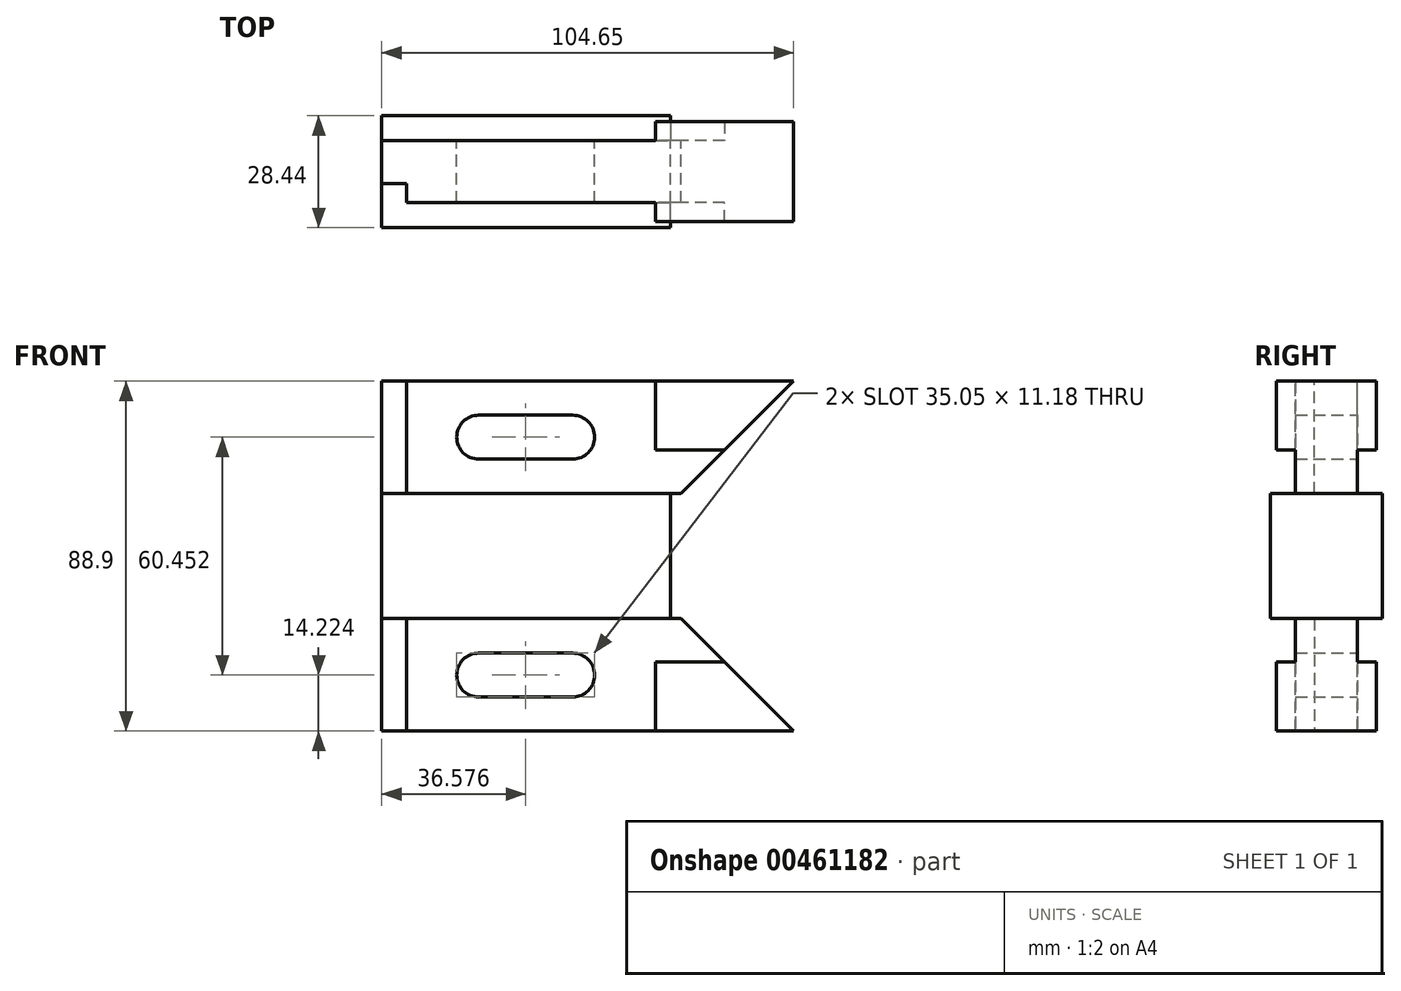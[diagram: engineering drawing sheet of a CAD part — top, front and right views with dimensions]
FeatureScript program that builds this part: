
annotation { "Feature Type Name" : "Feature", "Feature Type Description" : "" }
export const myFeature = defineFeature(function(context is Context, id is Id, definition is map)
    precondition{}
    {
        {
            var Q0;
            Q0=qCreatedBy(makeId("Front.planeOp"),FACE);
            var sketch = newSketch(context, id + "F0", { "sketchPlane" : qUnion([Q0])});
            skLineSegment(sketch, "E0", {"start": v(0, 0) * mm, "end": v(0, 44.45) * mm});
            skLineSegment(sketch, "E1", {"start": v(0, 44.45) * mm, "end": v(104.65, 44.45) * mm});
            skLineSegment(sketch, "E2", {"start": v(104.65, 44.45) * mm, "end": v(76.07, 15.88) * mm});
            skLineSegment(sketch, "E3", {"start": v(76.07, 15.88) * mm, "end": v(0, 15.88) * mm});
            skLineSegment(sketch, "E4", {"start": v(0, 0) * mm, "end": v(94.14, 0) * mm});
            skArc(sketch, "E5", {"start": v(24.64, 35.81) * mm, "mid": v(19.05, 30.23) * mm, "end": v(24.64, 24.64) * mm});
            skArc(sketch, "E6", {"start": v(48.51, 24.64) * mm, "mid": v(54.1, 30.23) * mm, "end": v(48.51, 35.81) * mm});
            skLineSegment(sketch, "E7", {"start": v(24.64, 35.81) * mm, "end": v(48.51, 35.81) * mm});
            skLineSegment(sketch, "E8", {"start": v(24.64, 24.64) * mm, "end": v(48.51, 24.64) * mm});
            skLineSegment(sketch, "E9", {"start": v(69.6, 44.45) * mm, "end": v(69.6, 26.92) * mm});
            skLineSegment(sketch, "E10", {"start": v(69.6, 26.92) * mm, "end": v(87.12, 26.92) * mm});
            skLineSegment(sketch, "E11", {"start": v(6.35, 44.45) * mm, "end": v(6.35, 15.88) * mm});
            skLineSegment(sketch, "E12", {"start": v(24.64, 30.23) * mm, "end": v(48.51, 30.23) * mm, "construction": true});
            skLineSegment(sketch, "E13", {"start": v(-38.06, 0) * mm, "end": v(126.35, 0) * mm, "construction": true});
            skLineSegment(sketch, "E14.MirrorCS", {"start": v(6.35, -44.45) * mm, "end": v(6.35, -15.88) * mm});
            skArc(sketch, "E15.MirrorCS", {"start": v(48.51, -24.64) * mm, "mid": v(54.1, -30.23) * mm, "end": v(48.51, -35.81) * mm});
            skLineSegment(sketch, "E16.MirrorCS", {"start": v(69.6, -26.92) * mm, "end": v(87.12, -26.92) * mm});
            skLineSegment(sketch, "E17.MirrorCS", {"start": v(104.65, -44.45) * mm, "end": v(76.07, -15.88) * mm});
            skArc(sketch, "E18.MirrorCS", {"start": v(24.64, -35.81) * mm, "mid": v(19.05, -30.23) * mm, "end": v(24.64, -24.64) * mm});
            skLineSegment(sketch, "E19.MirrorCS", {"start": v(0, -44.45) * mm, "end": v(104.65, -44.45) * mm});
            skLineSegment(sketch, "E20.MirrorCS", {"start": v(24.64, -24.64) * mm, "end": v(48.51, -24.64) * mm});
            skLineSegment(sketch, "E21.MirrorCS", {"start": v(24.64, -35.81) * mm, "end": v(48.51, -35.81) * mm});
            skLineSegment(sketch, "E22.MirrorCS", {"start": v(24.64, -30.23) * mm, "end": v(48.51, -30.23) * mm, "construction": true});
            skLineSegment(sketch, "E23.MirrorCS", {"start": v(69.6, -44.45) * mm, "end": v(69.6, -26.92) * mm});
            skLineSegment(sketch, "E24.MirrorCS", {"start": v(76.07, -15.88) * mm, "end": v(0, -15.88) * mm});
            skLineSegment(sketch, "E25.MirrorCS", {"start": v(0, 0) * mm, "end": v(0, -44.45) * mm});
            skLineSegment(sketch, "E26", {"start": v(73.4, -15.87) * mm, "end": v(73.4, 15.87) * mm});
            skSolve(sketch);
        }
        {
            var Q0;
            Q0 = qSketchRegion(id + "F0", true);
            extrude(context, id + "F1", {"entities" : qUnion([Q0]), "depth" : 7.87 * mm});
        }
        {
            var Q0;
            {var subQ0=sQuery(id+"F0.wireOp",EDGE,"E4");Q0=makeQuery(id+"F0.imprint","IMPRINT",FACE,{"disambiguationData":[TD([[makeQuery(id+"F0.imprint","IMPRINT",EDGE,{"derivedFrom":subQ0}),1.0]])]});}
            var Q1;
            {var subQ1=sQuery(id+"F0.wireOp",EDGE,"E4");Q1=makeQuery(id+"F0.imprint","IMPRINT",FACE,{"disambiguationData":[TD([[makeQuery(id+"F0.imprint","IMPRINT",EDGE,{"derivedFrom":subQ1}),-1.0]])]});}
            extrude(context, id + "F2", {"entities" : qUnion([Q0, Q1]), "operationType" : NewBodyOperationType.ADD, "depth" : 14.22 * mm});
        }
        {
            var Q0;
            {var subQ3=sQuery(id+"F0.wireOp",EDGE,"E9");Q0=makeQuery(id+"F0.imprint","IMPRINT",FACE,{"disambiguationData":[TD([[makeQuery(id+"F0.imprint","IMPRINT",EDGE,{"derivedFrom":subQ3}),1.0]])]});}
            var Q1;
            {var subQ0=sQuery(id+"F0.wireOp",EDGE,"E16.MirrorCS");Q1=makeQuery(id+"F0.imprint","IMPRINT",FACE,{"disambiguationData":[TD([[makeQuery(id+"F0.imprint","IMPRINT",EDGE,{"derivedFrom":subQ0}),-1.0]])]});}
            extrude(context, id + "F3", {"entities" : qUnion([Q0, Q1]), "operationType" : NewBodyOperationType.ADD, "depth" : 12.7 * mm});
        }
        {
            var Q0;
            Q0=makeQuery(id+"F1.opExtrude","SWEPT_BODY",BODY,{"disambiguationData":[OSD([sQuery(id+"F0.wireOp",EDGE,"E0"),sQuery(id+"F0.wireOp",EDGE,"E1"),sQuery(id+"F0.wireOp",EDGE,"E2"),sQuery(id+"F0.wireOp",EDGE,"dfV1hQ6U-fgLX-1oEq-Cl2Z-QLcZu5KokJ9a"),sQuery(id+"F0.wireOp",EDGE,"E5"),sQuery(id+"F0.wireOp",EDGE,"E6"),sQuery(id+"F0.wireOp",EDGE,"E7"),sQuery(id+"F0.wireOp",EDGE,"E8"),sQuery(id+"F0.wireOp",EDGE,"E15.MirrorCS"),sQuery(id+"F0.wireOp",EDGE,"E17.MirrorCS"),sQuery(id+"F0.wireOp",EDGE,"E18.MirrorCS"),sQuery(id+"F0.wireOp",EDGE,"E19.MirrorCS"),sQuery(id+"F0.wireOp",EDGE,"E20.MirrorCS"),sQuery(id+"F0.wireOp",EDGE,"E21.MirrorCS"),sQuery(id+"F0.wireOp",EDGE,"E25.MirrorCS"),sQuery(id+"F0.wireOp",EDGE,"4e4c7bbf-45cc-40e8-b10d-9f1884ca9b700.MirrorCS")])]});
            var Q1;
            Q1=qCreatedBy(makeId("Front.planeOp"),FACE);
            mirror(context, id + "F4", {"operationType" : NewBodyOperationType.ADD, "entities" : qUnion([Q0]), "mirrorPlane" : qUnion([Q1])});
        }
        {
            var Q0;
            {var subQ0=sQuery(id+"F0.wireOp",EDGE,"E8");var subQ1=sQuery(id+"F0.wireOp",EDGE,"E7");var subQ2=sQuery(id+"F0.wireOp",EDGE,"E6");var subQ3=sQuery(id+"F0.wireOp",EDGE,"E25.MirrorCS");var subQ4=sQuery(id+"F0.wireOp",EDGE,"E0");var subQ5=sQuery(id+"F0.wireOp",EDGE,"E5");var subQ6=sQuery(id+"F0.wireOp",EDGE,"E1");var subQ7=sQuery(id+"F0.wireOp",EDGE,"E2");var subQ8=sQuery(id+"F0.wireOp",EDGE,"4e4c7bbf-45cc-40e8-b10d-9f1884ca9b700.MirrorCS");var subQ9=sQuery(id+"F0.wireOp",EDGE,"dfV1hQ6U-fgLX-1oEq-Cl2Z-QLcZu5KokJ9a");Q0=makeQuery(id+"F2.boolean.opBoolean","SPLIT",FACE,{"disambiguationData":[TD([makeQuery(id+"F1.opExtrude","SWEPT_FACE",FACE,{"disambiguationData":[OSD([subQ6])]})])],"derivedFrom":makeQuery(id+"F1.opExtrude","CAP_FACE",FACE,{"disambiguationData":[OSD([subQ4,subQ6,subQ7,subQ9,subQ5,subQ2,subQ1,subQ0,sQuery(id+"F0.wireOp",EDGE,"E15.MirrorCS"),sQuery(id+"F0.wireOp",EDGE,"E17.MirrorCS"),sQuery(id+"F0.wireOp",EDGE,"E18.MirrorCS"),sQuery(id+"F0.wireOp",EDGE,"E19.MirrorCS"),sQuery(id+"F0.wireOp",EDGE,"E20.MirrorCS"),sQuery(id+"F0.wireOp",EDGE,"E21.MirrorCS"),subQ3,subQ8])],"isStart":false})});}
            var sketch = newSketch(context, id + "F5", { "sketchPlane" : qUnion([Q0])});
            skLineSegment(sketch, "E27.0", {"start": v(6.35, 44.45) * mm, "end": v(6.35, 15.88) * mm});
            skLineSegment(sketch, "E28.0", {"start": v(6.35, -44.45) * mm, "end": v(6.35, -15.88) * mm});
            skLineSegment(sketch, "E29", {"start": v(6.35, 44.45) * mm, "end": v(0, 44.45) * mm});
            skLineSegment(sketch, "E30", {"start": v(0, 44.45) * mm, "end": v(0, 15.88) * mm});
            skLineSegment(sketch, "E31", {"start": v(0, 15.88) * mm, "end": v(6.35, 15.88) * mm});
            skLineSegment(sketch, "E32", {"start": v(6.35, -15.88) * mm, "end": v(0, -15.88) * mm});
            skLineSegment(sketch, "E33", {"start": v(0, -15.88) * mm, "end": v(0, -44.45) * mm});
            skLineSegment(sketch, "E34", {"start": v(0, -44.45) * mm, "end": v(6.35, -44.45) * mm});
            skSolve(sketch);
        }
        {
            var Q0;
            Q0 = qSketchRegion(id + "F5", true);
            extrude(context, id + "F6", {"entities" : qUnion([Q0]), "operationType" : NewBodyOperationType.REMOVE, "oppositeDirection" : true, "depth" : 4.83 * mm});
        }
    });
